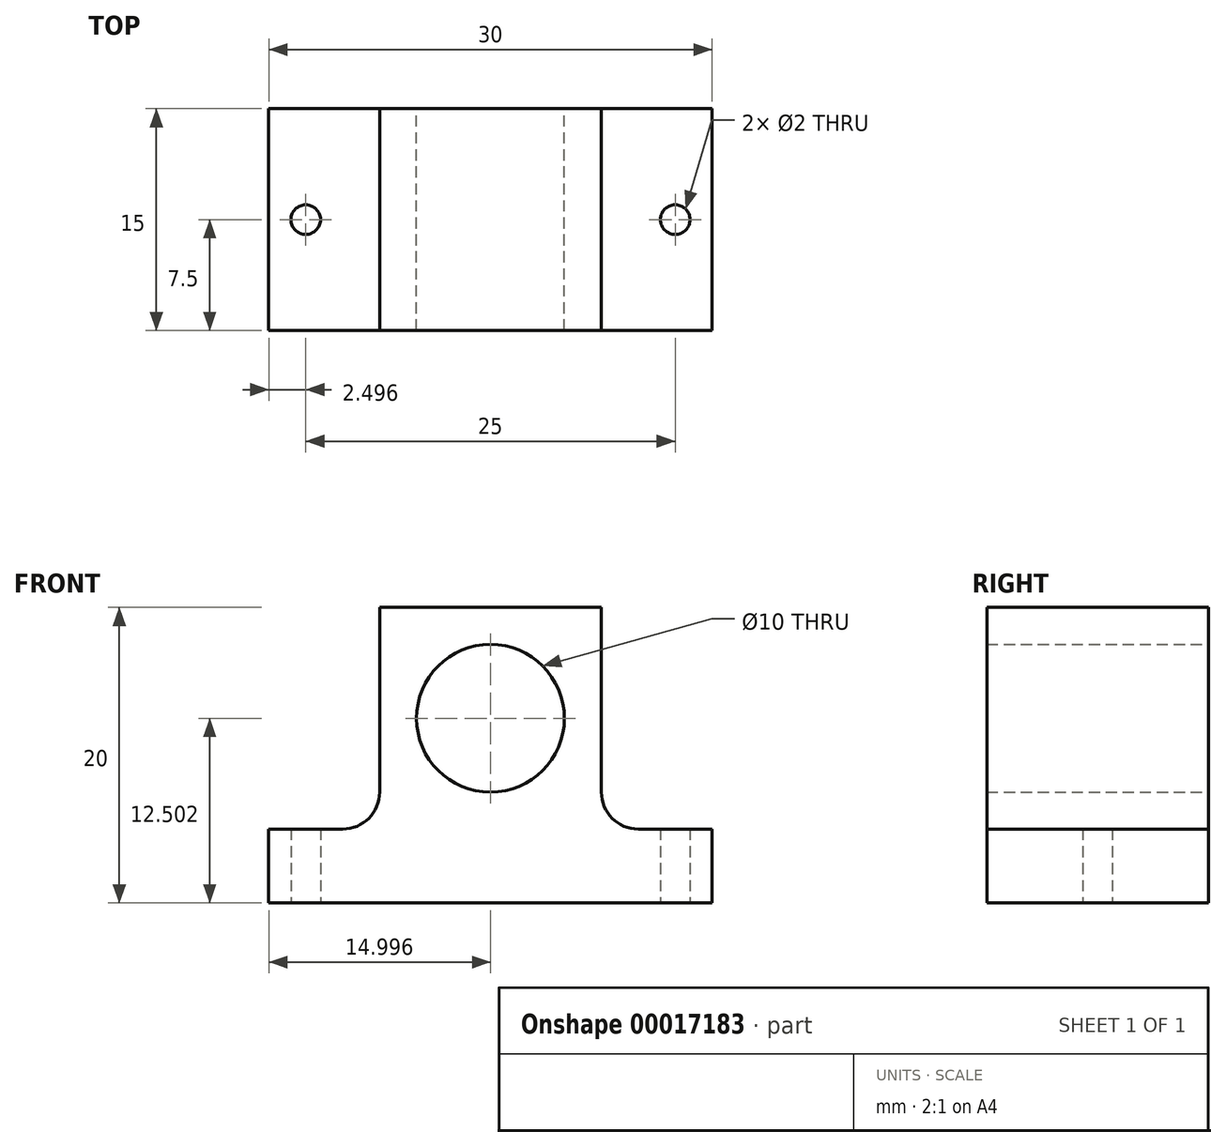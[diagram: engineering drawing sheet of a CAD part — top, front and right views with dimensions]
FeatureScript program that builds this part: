
annotation { "Feature Type Name" : "Feature", "Feature Type Description" : "" }
export const myFeature = defineFeature(function(context is Context, id is Id, definition is map)
    precondition{}
    {
        {
            var Q0;
            Q0=qCreatedBy(makeId("Front.planeOp"),FACE);
            var sketch = newSketch(context, id + "F0", { "sketchPlane" : qUnion([Q0])});
            skLineSegment(sketch, "E0", {"start": v(-18.17, 26.7) * mm, "end": v(-3.17, 26.7) * mm});
            skLineSegment(sketch, "E1", {"start": v(-18.17, 26.7) * mm, "end": v(-18.17, 14.2) * mm});
            skLineSegment(sketch, "E2", {"start": v(-3.17, 26.7) * mm, "end": v(-3.17, 14.2) * mm});
            skLineSegment(sketch, "E3", {"start": v(-20.67, 11.7) * mm, "end": v(-25.67, 11.7) * mm});
            skLineSegment(sketch, "E4", {"start": v(-0.67, 11.7) * mm, "end": v(4.33, 11.7) * mm});
            skLineSegment(sketch, "E5", {"start": v(-25.67, 11.7) * mm, "end": v(-25.67, 6.7) * mm});
            skLineSegment(sketch, "E6", {"start": v(-25.67, 6.7) * mm, "end": v(4.33, 6.7) * mm});
            skLineSegment(sketch, "E7", {"start": v(4.33, 6.7) * mm, "end": v(4.33, 11.7) * mm});
            skPoint(sketch, "E8.visualSharp", {"position": v(-3.17, 11.7) * mm});
            skArc(sketch, "E8.filletArc", {"start": v(-3.17, 14.2) * mm, "mid": v(-2.44, 12.42) * mm, "end": v(-0.67, 11.7) * mm});
            skPoint(sketch, "E9.visualSharp", {"position": v(-18.17, 11.7) * mm});
            skArc(sketch, "E9.filletArc", {"start": v(-20.67, 11.7) * mm, "mid": v(-18.9, 12.42) * mm, "end": v(-18.17, 14.2) * mm});
            skSolve(sketch);
        }
        {
            var Q0;
            Q0=qCreatedBy(makeId("Front.planeOp"),FACE);
            var sketch = newSketch(context, id + "F1", { "sketchPlane" : qUnion([Q0])});
            skCircle(sketch, "E10", {"center": v(-10.67, 19.2) * mm, "radius": 5 * mm});
            skSolve(sketch);
        }
        {
            var Q0;
            Q0=makeQuery(id+"F0.imprint","IMPRINT",FACE,{"disambiguationData":[TD([[makeQuery(id+"F0.imprint","IMPRINT",EDGE,{"derivedFrom":sQuery(id+"F0.wireOp",EDGE,"E0")}),-1.0]])]});
            extrude(context, id + "F2", {"entities" : qUnion([Q0]), "depth" : 15 * mm});
        }
        {
            var Q0;
            Q0 = qSketchRegion(id + "F1", true);
            extrude(context, id + "F3", {"entities" : qUnion([Q0]), "operationType" : NewBodyOperationType.REMOVE, "depth" : 15 * mm});
        }
        {
            var Q0;
            Q0=qCreatedBy(makeId("Top.planeOp"),FACE);
            var sketch = newSketch(context, id + "F4", { "sketchPlane" : qUnion([Q0])});
            skCircle(sketch, "E11", {"center": v(1.83, -7.5) * mm, "radius": 1 * mm});
            skCircle(sketch, "E12", {"center": v(-23.17, -7.5) * mm, "radius": 1 * mm});
            skSolve(sketch);
        }
        {
            var Q0;
            Q0 = qSketchRegion(id + "F4", true);
            extrude(context, id + "F5", {"entities" : qUnion([Q0]), "operationType" : NewBodyOperationType.REMOVE, "depth" : 15 * mm});
        }
    });
